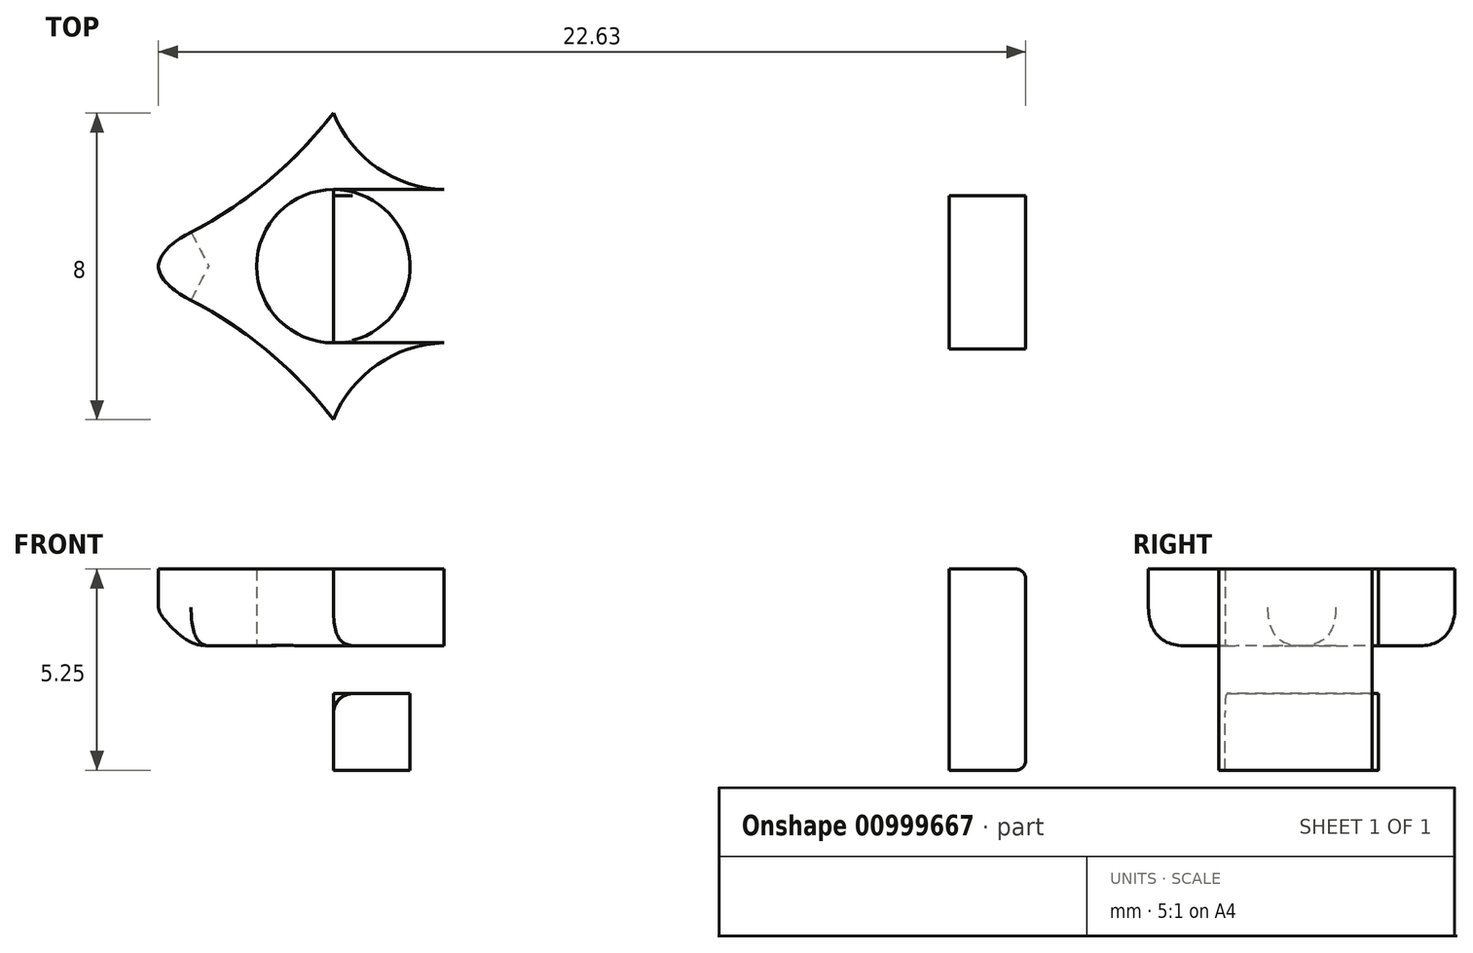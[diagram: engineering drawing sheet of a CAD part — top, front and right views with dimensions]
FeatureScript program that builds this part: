
annotation { "Feature Type Name" : "Feature", "Feature Type Description" : "" }
export const myFeature = defineFeature(function(context is Context, id is Id, definition is map)
    precondition{}
    {
        {
            assignVariable(context, id + "F0", {"name" : "ct", "anyValue" : 1.25});
        }
        {
            assignVariable(context, id + "F1", {"name" : "w", "anyValue" : 4});
        }
        {
            assignVariable(context, id + "F2", {"name" : "t", "anyValue" : 2});
        }
        {
            var Q0;
            Q0=qCreatedBy(makeId("Top.planeOp"),FACE);
            var sketch = newSketch(context, id + "F3", { "sketchPlane" : qUnion([Q0])});
            skLineSegment(sketch, "E0.left", {"start": v(0, 0) * mm, "end": v(0, 4) * mm});
            skLineSegment(sketch, "E0.right", {"start": v(-16.06, 0.16) * mm, "end": v(-16.06, 4.16) * mm});
            skLineSegment(sketch, "E1", {"start": v(-16.06, 2.16) * mm, "end": v(-22.06, 2.16) * mm, "construction": true});
            skCircle(sketch, "E2", {"center": v(-16.06, 2.16) * mm, "radius": 2 * mm});
            skLineSegment(sketch, "E3", {"start": v(-16.06, 4.16) * mm, "end": v(-16.06, 6.16) * mm, "construction": true});
            skLineSegment(sketch, "E4", {"start": v(0, 2) * mm, "end": v(-16.06, 2.16) * mm, "construction": true});
            skArc(sketch, "E5", {"start": v(-22.06, 2.16) * mm, "mid": v(-18.73, 3.67) * mm, "end": v(-16.06, 6.16) * mm});
            skArc(sketch, "E6.MirrorCS", {"start": v(-22.06, 2.16) * mm, "mid": v(-18.73, 0.66) * mm, "end": v(-16.06, -1.84) * mm});
            skLineSegment(sketch, "E7.bottom", {"start": v(0, 4) * mm, "end": v(2, 4) * mm});
            skLineSegment(sketch, "E7.top", {"start": v(0, 0) * mm, "end": v(2, 0) * mm});
            skLineSegment(sketch, "E7.left", {"start": v(0, 4) * mm, "end": v(0, 0) * mm});
            skLineSegment(sketch, "E7.right", {"start": v(2, 4) * mm, "end": v(2, 0) * mm});
            skLineSegment(sketch, "E8", {"start": v(-14.68, 4.58) * mm, "end": v(-15.07, 3.9) * mm, "construction": true});
            skLineSegment(sketch, "E9", {"start": v(-15.07, 0.43) * mm, "end": v(-14.68, -0.25) * mm, "construction": true});
            skLineSegment(sketch, "E10", {"start": v(0, 4) * mm, "end": v(-13.18, 4.16) * mm});
            skLineSegment(sketch, "E11", {"start": v(-13.18, 0.16) * mm, "end": v(0, 0) * mm});
            skLineSegment(sketch, "E12", {"start": v(-13.18, 4.16) * mm, "end": v(-13.18, 0.16) * mm, "construction": true});
            skLineSegment(sketch, "E13", {"start": v(-16.06, 4.16) * mm, "end": v(-13.18, 4.16) * mm});
            skLineSegment(sketch, "E14", {"start": v(-16.06, 0.16) * mm, "end": v(-13.18, 0.16) * mm});
            skLineSegment(sketch, "E15", {"start": v(-16.06, 0.16) * mm, "end": v(-16.06, -1.84) * mm, "construction": true});
            skArc(sketch, "E16", {"start": v(-13.18, 0.16) * mm, "mid": v(-14.92, -0.4) * mm, "end": v(-16.06, -1.84) * mm});
            skLineSegment(sketch, "E17", {"start": v(-17.33, 0.62) * mm, "end": v(-17.84, 0) * mm, "construction": true});
            skLineSegment(sketch, "E18", {"start": v(-17.33, 3.71) * mm, "end": v(-17.84, 4.33) * mm, "construction": true});
            skArc(sketch, "E19", {"start": v(-16.06, 6.16) * mm, "mid": v(-14.92, 4.74) * mm, "end": v(-13.18, 4.16) * mm});
            skSolve(sketch);
        }
        {
            var Q0;
            Q0=makeQuery(id+"F3.imprint","IMPRINT",FACE,{"disambiguationData":[TD([[makeQuery(id+"F3.imprint","IMPRINT",EDGE,{"derivedFrom":sQuery(id+"F3.wireOp",EDGE,"E5")}),-1.0]])]});
            var Q1;
            {var subQ4=sQuery(id+"F3.wireOp",EDGE,"E7.left");Q1=makeQuery(id+"F3.imprint","IMPRINT",FACE,{"disambiguationData":[TD([[makeQuery(id+"F3.imprint","IMPRINT",EDGE,{"derivedFrom":subQ4}),-1.0]])]});}
            var Q2;
            Q2=makeQuery(id+"F3.imprint","IMPRINT",FACE,{"disambiguationData":[TD([[makeQuery(id+"F3.imprint","IMPRINT",EDGE,{"derivedFrom":sQuery(id+"F3.wireOp",EDGE,"E7.bottom")}),-1.0]])]});
            extrude(context, id + "F4", {"entities" : qUnion([Q0, Q1, Q2]), "depth" : (getVariable(context, 't')) * mm, "offsetDistance" : 25 * mm});
        }
        {
            var Q0;
            Q0=makeQuery(id+"F3.imprint","IMPRINT",FACE,{"disambiguationData":[TD([[makeQuery(id+"F3.imprint","IMPRINT",EDGE,{"derivedFrom":sQuery(id+"F3.wireOp",EDGE,"E7.bottom")}),-1.0]])]});
            extrude(context, id + "F5", {"entities" : qUnion([Q0]), "operationType" : NewBodyOperationType.ADD, "oppositeDirection" : true, "depth" : (getVariable(context, 'ct')) * mm, "offsetDistance" : 25 * mm});
        }
        {
            var Q0;
            {var subQ0=sQuery(id+"F3.wireOp",EDGE,"E0.right");Q0=makeQuery(id+"F3.imprint","IMPRINT",FACE,{"disambiguationData":[TD([[makeQuery(id+"F3.imprint","IMPRINT",EDGE,{"derivedFrom":subQ0}),-1.0]])]});}
            var Q1;
            {var subQ4=sQuery(id+"F3.wireOp",EDGE,"E7.left");Q1=makeQuery(id+"F3.imprint","IMPRINT",FACE,{"disambiguationData":[TD([[makeQuery(id+"F3.imprint","IMPRINT",EDGE,{"derivedFrom":subQ4}),-1.0]])]});}
            var Q2;
            Q2=makeQuery(id+"F3.imprint","IMPRINT",FACE,{"disambiguationData":[TD([[makeQuery(id+"F3.imprint","IMPRINT",EDGE,{"derivedFrom":sQuery(id+"F3.wireOp",EDGE,"E7.bottom")}),-1.0]])]});
            extrude(context, id + "F6", {"entities" : qUnion([Q0, Q1, Q2]), "operationType" : NewBodyOperationType.ADD, "oppositeDirection" : true, "depth" : (getVariable(context, 'ct') + getVariable(context, 't')) * mm, "offsetDistance" : 25 * mm, "hasSecondDirection" : true, "secondDirectionOppositeDirection" : true, "secondDirectionDepth" : (getVariable(context, 'ct')) * mm});
        }
        {
            var Q0;
            Q0=makeQuery(id+"F4.opExtrude","CAP_EDGE",EDGE,{"disambiguationData":[OSD([sQuery(id+"F3.wireOp",EDGE,"E6.MirrorCS")])],"isStart":true});
            fillet(context, id + "F7", {"entities" : qUnion([Q0]), "radius" : 1 * mm, "tangentPropagation" : true, "rho" : 0.5, "crossSection" : FilletCrossSection.CONIC, "allowEdgeOverflow" : false});
        }
        {
            var Q0;
            Q0=qCreatedBy(makeId("Front.planeOp"),FACE);
            var sketch = newSketch(context, id + "F8", { "sketchPlane" : qUnion([Q0])});
            skLineSegment(sketch, "E20.bottom", {"start": v(-22, 1.73) * mm, "end": v(-16, 1.73) * mm});
            skLineSegment(sketch, "E20.top", {"start": v(-21.5, 0) * mm, "end": v(-16, 0) * mm});
            skLineSegment(sketch, "E20.left", {"start": v(-22, 1.73) * mm, "end": v(-22, 0.5) * mm});
            skLineSegment(sketch, "E20.right", {"start": v(-16, 1.73) * mm, "end": v(-16, 0) * mm});
            skPoint(sketch, "E21.visualSharp", {"position": v(-22, 0) * mm});
            skArc(sketch, "E21.filletArc", {"start": v(-22, 0.5) * mm, "mid": v(-21.85, 0.15) * mm, "end": v(-21.5, 0) * mm});
            skLineSegment(sketch, "E22.bottom", {"start": v(-21.5, 0.5) * mm, "end": v(-22, 0.5) * mm});
            skLineSegment(sketch, "E22.top", {"start": v(-21.5, 0) * mm, "end": v(-22, 0) * mm});
            skLineSegment(sketch, "E22.left", {"start": v(-21.5, 0.5) * mm, "end": v(-21.5, 0) * mm});
            skLineSegment(sketch, "E22.right", {"start": v(-22, 0.5) * mm, "end": v(-22, 0) * mm});
            skSolve(sketch);
        }
        {
            var Q0;
            Q0=makeQuery(id+"F8.imprint","IMPRINT",FACE,{"disambiguationData":[TD([[makeQuery(id+"F8.imprint","IMPRINT",EDGE,{"derivedFrom":sQuery(id+"F8.wireOp",EDGE,"E21.filletArc")}),-1.0]])]});
            extrude(context, id + "F9", {"entities" : qUnion([Q0]), "operationType" : NewBodyOperationType.REMOVE, "oppositeDirection" : true, "depth" : 6.6 * mm, "offsetDistance" : 25 * mm});
        }
        {
            var Q0;
            {var subQ0=sQuery(id+"F3.wireOp",EDGE,"E7.top");var subQ1=sQuery(id+"F3.wireOp",EDGE,"E0.bottom");Q0=makeQuery(id+"F6.boolean.opBoolean","MERGE",FACE,{"derivedFrom":[makeQuery(id+"F5.boolean.opBoolean","MERGE",FACE,{"derivedFrom":[makeQuery(id+"F4.opExtrude","SWEPT_FACE",FACE,{"disambiguationData":[OSD([subQ1,subQ0])]}),makeQuery(id+"F5.opExtrude","SWEPT_FACE",FACE,{"disambiguationData":[OSD([subQ0])]})]}),makeQuery(id+"F6.opExtrude","SWEPT_FACE",FACE,{"disambiguationData":[OSD([subQ1,subQ0])]})]});}
            var sketch = newSketch(context, id + "F10", { "sketchPlane" : qUnion([Q0])});
            skLineSegment(sketch, "E23.bottom", {"start": v(-15.56, -1.25) * mm, "end": v(-14.68, -1.25) * mm});
            skLineSegment(sketch, "E23.top", {"start": v(-16.06, -3.25) * mm, "end": v(-14.68, -3.25) * mm});
            skLineSegment(sketch, "E23.left", {"start": v(-16.06, -1.75) * mm, "end": v(-16.06, -3.25) * mm});
            skLineSegment(sketch, "E23.right", {"start": v(-14.68, -1.25) * mm, "end": v(-14.68, -3.25) * mm});
            skPoint(sketch, "E24.visualSharp", {"position": v(-16.06, -1.25) * mm});
            skArc(sketch, "E24.filletArc", {"start": v(-15.56, -1.25) * mm, "mid": v(-15.92, -1.4) * mm, "end": v(-16.06, -1.75) * mm});
            skLineSegment(sketch, "E25.bottom", {"start": v(1.75, 2) * mm, "end": v(0.76, 2) * mm});
            skLineSegment(sketch, "E25.top", {"start": v(1.75, -3.25) * mm, "end": v(0.76, -3.25) * mm});
            skLineSegment(sketch, "E25.left", {"start": v(2, 1.75) * mm, "end": v(2, -3) * mm});
            skLineSegment(sketch, "E25.right", {"start": v(0.76, 2) * mm, "end": v(0.76, -3.25) * mm});
            skPoint(sketch, "E26.visualSharp", {"position": v(2, 2) * mm});
            skArc(sketch, "E26.filletArc", {"start": v(2, 1.75) * mm, "mid": v(1.93, 1.93) * mm, "end": v(1.75, 2) * mm});
            skPoint(sketch, "E27.visualSharp", {"position": v(2, -3.25) * mm});
            skArc(sketch, "E27.filletArc", {"start": v(1.75, -3.25) * mm, "mid": v(1.93, -3.18) * mm, "end": v(2, -3) * mm});
            skLineSegment(sketch, "E28.bottom", {"start": v(-16.06, -1.25) * mm, "end": v(-15.56, -1.25) * mm});
            skLineSegment(sketch, "E28.top", {"start": v(-16.06, -1.75) * mm, "end": v(-15.56, -1.75) * mm});
            skLineSegment(sketch, "E28.left", {"start": v(-16.06, -1.25) * mm, "end": v(-16.06, -1.75) * mm});
            skLineSegment(sketch, "E28.right", {"start": v(-15.56, -1.25) * mm, "end": v(-15.56, -1.75) * mm});
            skSolve(sketch);
        }
        {
            var Q0;
            {var subQ0=sQuery(id+"F10.wireOp",EDGE,"E26.filletArc");Q0=makeQuery(id+"F10.imprint","IMPRINT",FACE,{"disambiguationData":[TD([[makeQuery(id+"F10.imprint","IMPRINT",EDGE,{"derivedFrom":subQ0}),-1.0]])]});}
            var Q1;
            {var subQ0=sQuery(id+"F10.wireOp",EDGE,"E27.filletArc");Q1=makeQuery(id+"F10.imprint","IMPRINT",FACE,{"disambiguationData":[TD([[makeQuery(id+"F10.imprint","IMPRINT",EDGE,{"derivedFrom":subQ0}),-1.0]])]});}
            extrude(context, id + "F11", {"entities" : qUnion([Q0, Q1]), "operationType" : NewBodyOperationType.REMOVE, "oppositeDirection" : true, "depth" : (getVariable(context, 'w')) * mm, "offsetDistance" : 25 * mm});
        }
        {
            var Q0;
            Q0=makeQuery(id+"F10.imprint","IMPRINT",FACE,{"disambiguationData":[TD([[makeQuery(id+"F10.imprint","IMPRINT",EDGE,{"derivedFrom":sQuery(id+"F10.wireOp",EDGE,"E24.filletArc")}),-1.0]])]});
            extrude(context, id + "F12", {"entities" : qUnion([Q0]), "operationType" : NewBodyOperationType.REMOVE, "oppositeDirection" : true, "depth" : (getVariable(context, 'w')) * mm, "offsetDistance" : 25 * mm});
        }
        {
            var Q0;
            Q0=makeQuery(id+"F4.opExtrude","CAP_EDGE",EDGE,{"disambiguationData":[OSD([sQuery(id+"F3.wireOp",EDGE,"E5")])],"isStart":true});
            fillet(context, id + "F13", {"entities" : qUnion([Q0]), "radius" : 1 * mm, "tangentPropagation" : true, "rho" : 0.5, "crossSection" : FilletCrossSection.CONIC, "allowEdgeOverflow" : false});
        }
    });
